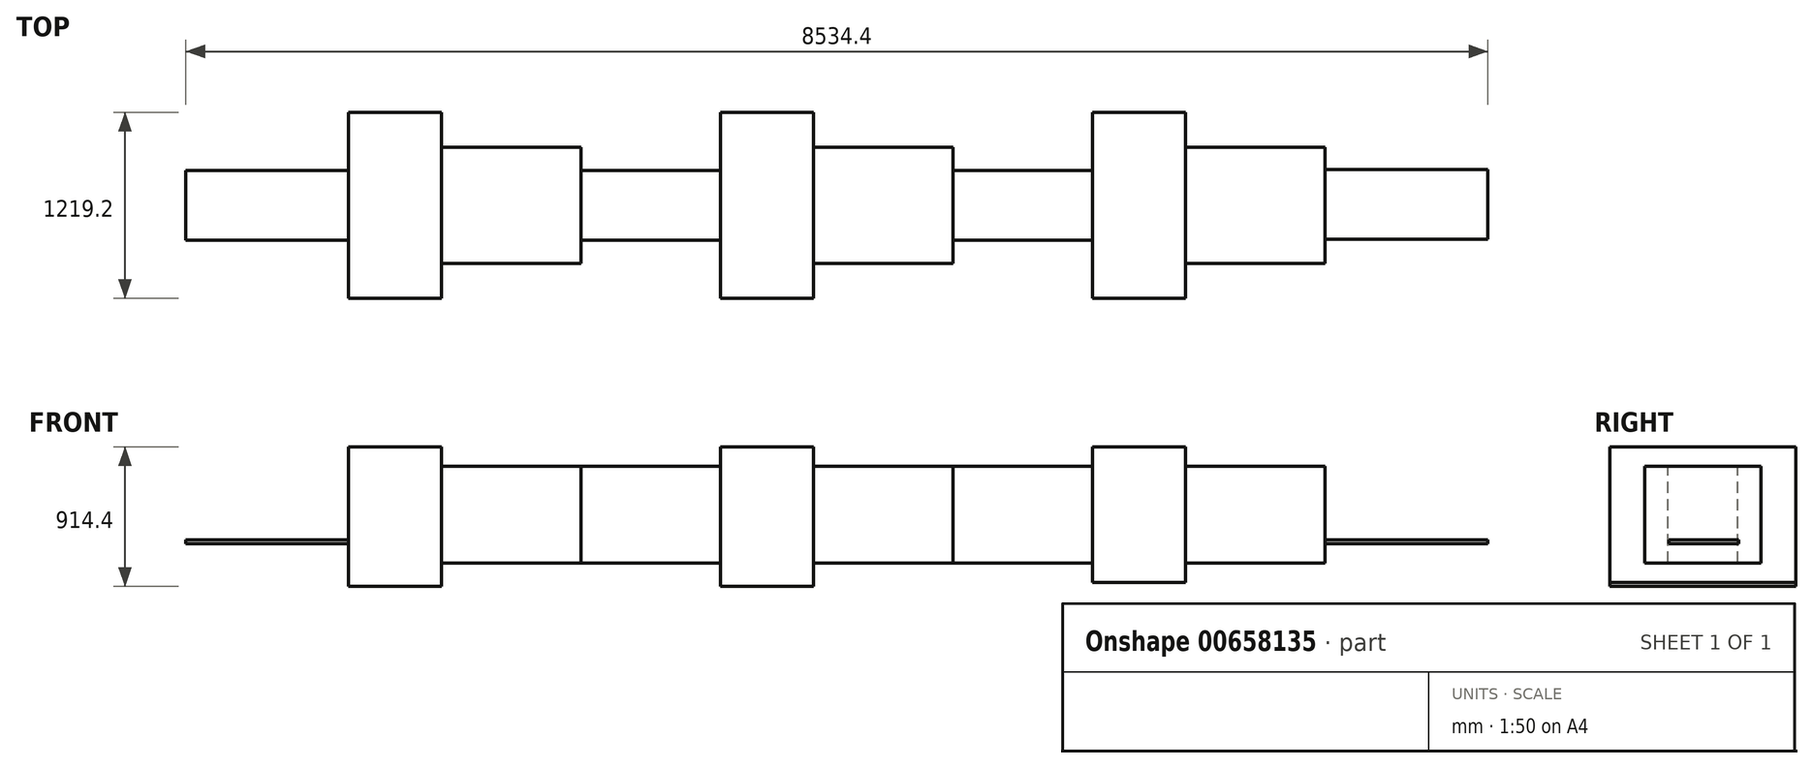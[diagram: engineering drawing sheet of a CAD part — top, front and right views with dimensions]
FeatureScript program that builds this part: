
annotation { "Feature Type Name" : "Feature", "Feature Type Description" : "" }
export const myFeature = defineFeature(function(context is Context, id is Id, definition is map)
    precondition{}
    {
        {
            var Q0;
            Q0=qCreatedBy(makeId("Top.planeOp"),FACE);
            var sketch = newSketch(context, id + "F0", { "sketchPlane" : qUnion([Q0])});
            skLineSegment(sketch, "E0.bottom", {"start": v(0, 0) * mm, "end": v(1066.8, 0) * mm});
            skLineSegment(sketch, "E0.top", {"start": v(0, 457.2) * mm, "end": v(1066.8, 457.2) * mm});
            skLineSegment(sketch, "E0.left", {"start": v(0, 0) * mm, "end": v(0, 457.2) * mm});
            skLineSegment(sketch, "E0.right", {"start": v(1066.8, 0) * mm, "end": v(1066.8, 457.2) * mm});
            skSolve(sketch);
        }
        {
            var Q0;
            Q0 = qSketchRegion(id + "F0", true);
            extrude(context, id + "F1", {"entities" : qUnion([Q0]), "depth" : 25.4 * mm, "offsetDistance" : 25.4 * mm});
        }
        {
            var Q0;
            Q0=makeQuery(id+"F1.opExtrude","CAP_FACE",FACE,{"disambiguationData":[OSD([sQuery(id+"F0.wireOp",EDGE,"E0.bottom"),sQuery(id+"F0.wireOp",EDGE,"E0.top"),sQuery(id+"F0.wireOp",EDGE,"E0.left"),sQuery(id+"F0.wireOp",EDGE,"E0.right")])],"isStart":false});
            var sketch = newSketch(context, id + "F2", { "sketchPlane" : qUnion([Q0])});
            skPoint(sketch, "E1", {"position": v(1066.8, -381) * mm});
            skLineSegment(sketch, "E2.bottom", {"start": v(1066.8, -381) * mm, "end": v(1676.4, -381) * mm});
            skLineSegment(sketch, "E2.top", {"start": v(1066.8, 838.2) * mm, "end": v(1676.4, 838.2) * mm});
            skLineSegment(sketch, "E2.left", {"start": v(1066.8, -381) * mm, "end": v(1066.8, 838.2) * mm});
            skLineSegment(sketch, "E2.right", {"start": v(1676.4, -381) * mm, "end": v(1676.4, 838.2) * mm});
            skSolve(sketch);
        }
        {
            var Q0;
            Q0 = qSketchRegion(id + "F2", true);
            extrude(context, id + "F3", {"entities" : qUnion([Q0]), "depth" : 609.6 * mm, "offsetDistance" : 25.4 * mm, "hasSecondDirection" : true, "secondDirectionOppositeDirection" : true, "secondDirectionDepth" : 304.8 * mm});
        }
        {
            var Q0;
            Q0=makeQuery(id+"F3.opExtrude","CAP_FACE",FACE,{"disambiguationData":[OSD([sQuery(id+"F2.wireOp",EDGE,"E2.bottom"),sQuery(id+"F2.wireOp",EDGE,"E2.top"),sQuery(id+"F2.wireOp",EDGE,"E2.left"),sQuery(id+"F2.wireOp",EDGE,"E2.right")])],"isStart":false});
            var sketch = newSketch(context, id + "F4", { "sketchPlane" : qUnion([Q0])});
            skLineSegment(sketch, "E3.right", {"start": v(2590.8, 0) * mm, "end": v(2590.8, 457.2) * mm});
            skPoint(sketch, "E4", {"position": v(2590.8, 0) * mm});
            skLineSegment(sketch, "E5.bottom", {"start": v(2590.8, 0) * mm, "end": v(3505.2, 0) * mm});
            skLineSegment(sketch, "E5.top", {"start": v(2590.8, 457.2) * mm, "end": v(3505.2, 457.2) * mm});
            skLineSegment(sketch, "E5.right", {"start": v(3505.2, 0) * mm, "end": v(3505.2, 457.2) * mm});
            skSolve(sketch);
        }
        {
            var Q0;
            Q0 = qSketchRegion(id + "F4", true);
            extrude(context, id + "F5", {"entities" : qUnion([Q0]), "oppositeDirection" : true, "depth" : 762 * mm, "offsetDistance" : 25.4 * mm, "hasSecondDirection" : true, "secondDirectionOppositeDirection" : true, "secondDirectionDepth" : 127 * mm});
        }
        {
            var Q0;
            Q0=makeQuery(id+"F3.opExtrude","CAP_FACE",FACE,{"disambiguationData":[OSD([sQuery(id+"F2.wireOp",EDGE,"E2.bottom"),sQuery(id+"F2.wireOp",EDGE,"E2.top"),sQuery(id+"F2.wireOp",EDGE,"E2.left"),sQuery(id+"F2.wireOp",EDGE,"E2.right")])],"isStart":false});
            var sketch = newSketch(context, id + "F6", { "sketchPlane" : qUnion([Q0])});
            skPoint(sketch, "E6", {"position": v(1676.4, -152.4) * mm});
            skPoint(sketch, "E7", {"position": v(1676.4, 228.6) * mm});
            skLineSegment(sketch, "E8.bottom", {"start": v(1676.4, -152.4) * mm, "end": v(2590.8, -152.4) * mm});
            skLineSegment(sketch, "E8.top", {"start": v(1676.4, 609.6) * mm, "end": v(2590.8, 609.6) * mm});
            skLineSegment(sketch, "E8.left", {"start": v(1676.4, -152.4) * mm, "end": v(1676.4, 609.6) * mm});
            skLineSegment(sketch, "E8.right", {"start": v(2590.8, -152.4) * mm, "end": v(2590.8, 609.6) * mm});
            skSolve(sketch);
        }
        {
            var Q0;
            Q0=makeQuery(id+"F6.imprint","IMPRINT",FACE,{"disambiguationData":[TD([[makeQuery(id+"F6.imprint","IMPRINT",EDGE,{"derivedFrom":sQuery(id+"F6.wireOp",EDGE,"E8.bottom")}),1.0]])]});
            extrude(context, id + "F7", {"entities" : qUnion([Q0]), "oppositeDirection" : true, "depth" : 762 * mm, "offsetDistance" : 25.4 * mm, "hasSecondDirection" : true, "secondDirectionOppositeDirection" : true, "secondDirectionDepth" : 127 * mm});
        }
        {
            var Q0;
            Q0=makeQuery(id+"F3.opExtrude","CAP_FACE",FACE,{"disambiguationData":[OSD([sQuery(id+"F2.wireOp",EDGE,"E2.bottom"),sQuery(id+"F2.wireOp",EDGE,"E2.top"),sQuery(id+"F2.wireOp",EDGE,"E2.left"),sQuery(id+"F2.wireOp",EDGE,"E2.right")])],"isStart":false});
            var sketch = newSketch(context, id + "F8", { "sketchPlane" : qUnion([Q0])});
            skPoint(sketch, "E9", {"position": v(3505.2, -381) * mm});
            skLineSegment(sketch, "E10.bottom", {"start": v(3505.2, -381) * mm, "end": v(4114.8, -381) * mm});
            skLineSegment(sketch, "E10.top", {"start": v(3505.2, 838.2) * mm, "end": v(4114.8, 838.2) * mm});
            skLineSegment(sketch, "E10.left", {"start": v(3505.2, -381) * mm, "end": v(3505.2, 838.2) * mm});
            skLineSegment(sketch, "E10.right", {"start": v(4114.8, -381) * mm, "end": v(4114.8, 838.2) * mm});
            skSolve(sketch);
        }
        {
            var Q0;
            Q0 = qSketchRegion(id + "F8", true);
            extrude(context, id + "F9", {"entities" : qUnion([Q0]), "oppositeDirection" : true, "depth" : 914.4 * mm, "offsetDistance" : 25.4 * mm});
        }
        {
            var Q0;
            Q0=makeQuery(id+"F9.opExtrude","CAP_FACE",FACE,{"disambiguationData":[OSD([sQuery(id+"F8.wireOp",EDGE,"E10.bottom"),sQuery(id+"F8.wireOp",EDGE,"E10.top"),sQuery(id+"F8.wireOp",EDGE,"E10.left"),sQuery(id+"F8.wireOp",EDGE,"E10.right")])],"isStart":true});
            var sketch = newSketch(context, id + "F10", { "sketchPlane" : qUnion([Q0])});
            skPoint(sketch, "E11", {"position": v(4114.8, -152.4) * mm});
            skPoint(sketch, "E12", {"position": v(4114.8, 228.6) * mm});
            skLineSegment(sketch, "E13.bottom", {"start": v(4114.8, -152.4) * mm, "end": v(5029.2, -152.4) * mm});
            skLineSegment(sketch, "E13.top", {"start": v(4114.8, 609.6) * mm, "end": v(5029.2, 609.6) * mm});
            skLineSegment(sketch, "E13.left", {"start": v(4114.8, -152.4) * mm, "end": v(4114.8, 609.6) * mm});
            skLineSegment(sketch, "E13.right", {"start": v(5029.2, -152.4) * mm, "end": v(5029.2, 609.6) * mm});
            skSolve(sketch);
        }
        {
            var Q0;
            Q0 = qSketchRegion(id + "F10", true);
            extrude(context, id + "F11", {"entities" : qUnion([Q0]), "oppositeDirection" : true, "depth" : 762 * mm, "offsetDistance" : 25.4 * mm, "hasSecondDirection" : true, "secondDirectionOppositeDirection" : true, "secondDirectionDepth" : 127 * mm});
        }
        {
            var Q0;
            Q0=makeQuery(id+"F11.opExtrude","CAP_FACE",FACE,{"disambiguationData":[OSD([sQuery(id+"F10.wireOp",EDGE,"E13.bottom"),sQuery(id+"F10.wireOp",EDGE,"E13.top"),sQuery(id+"F10.wireOp",EDGE,"E13.left"),sQuery(id+"F10.wireOp",EDGE,"E13.right")])],"isStart":true});
            var sketch = newSketch(context, id + "F12", { "sketchPlane" : qUnion([Q0])});
            skLineSegment(sketch, "E14.right", {"start": v(5029.2, 0) * mm, "end": v(5029.2, 457.2) * mm});
            skPoint(sketch, "E15", {"position": v(5029.2, 0) * mm});
            skLineSegment(sketch, "E16.bottom", {"start": v(5029.2, 0) * mm, "end": v(5943.6, 0) * mm});
            skLineSegment(sketch, "E16.top", {"start": v(5029.2, 457.2) * mm, "end": v(5943.6, 457.2) * mm});
            skLineSegment(sketch, "E16.right", {"start": v(5943.6, 0) * mm, "end": v(5943.6, 457.2) * mm});
            skSolve(sketch);
        }
        {
            var Q0;
            Q0 = qSketchRegion(id + "F12", true);
            extrude(context, id + "F13", {"entities" : qUnion([Q0]), "oppositeDirection" : true, "depth" : 635 * mm, "offsetDistance" : 25.4 * mm});
        }
        {
            var Q0;
            Q0=makeQuery(id+"F13.opExtrude","CAP_FACE",FACE,{"disambiguationData":[OSD([sQuery(id+"F12.wireOp",EDGE,"E16.bottom"),sQuery(id+"F12.wireOp",EDGE,"E16.top"),sQuery(id+"F12.wireOp",EDGE,"E14.right"),sQuery(id+"F12.wireOp",EDGE,"E16.right")])],"isStart":true});
            var sketch = newSketch(context, id + "F14", { "sketchPlane" : qUnion([Q0])});
            skPoint(sketch, "E17", {"position": v(5943.6, -381) * mm});
            skLineSegment(sketch, "E18.bottom", {"start": v(5943.6, -381) * mm, "end": v(6553.2, -381) * mm});
            skLineSegment(sketch, "E18.top", {"start": v(5943.6, 838.2) * mm, "end": v(6553.2, 838.2) * mm});
            skLineSegment(sketch, "E18.left", {"start": v(5943.6, -381) * mm, "end": v(5943.6, 838.2) * mm});
            skLineSegment(sketch, "E18.right", {"start": v(6553.2, -381) * mm, "end": v(6553.2, 838.2) * mm});
            skSolve(sketch);
        }
        {
            var Q0;
            Q0 = qSketchRegion(id + "F14", true);
            extrude(context, id + "F15", {"entities" : qUnion([Q0]), "depth" : 127 * mm, "offsetDistance" : 25.4 * mm, "hasSecondDirection" : true, "secondDirectionOppositeDirection" : true, "secondDirectionDepth" : 762 * mm});
        }
        {
            var Q0;
            Q0=makeQuery(id+"F15.opExtrude","CAP_FACE",FACE,{"disambiguationData":[OSD([sQuery(id+"F14.wireOp",EDGE,"E18.bottom"),sQuery(id+"F14.wireOp",EDGE,"E18.top"),sQuery(id+"F14.wireOp",EDGE,"E18.left"),sQuery(id+"F14.wireOp",EDGE,"E18.right")])],"isStart":false});
            var sketch = newSketch(context, id + "F16", { "sketchPlane" : qUnion([Q0])});
            skPoint(sketch, "E19", {"position": v(6553.2, -152.4) * mm});
            skPoint(sketch, "E20", {"position": v(6553.2, 228.6) * mm});
            skLineSegment(sketch, "E21.bottom", {"start": v(6553.2, -152.4) * mm, "end": v(7467.6, -152.4) * mm});
            skLineSegment(sketch, "E21.top", {"start": v(6553.2, 609.6) * mm, "end": v(7467.6, 609.6) * mm});
            skLineSegment(sketch, "E21.left", {"start": v(6553.2, -152.4) * mm, "end": v(6553.2, 609.6) * mm});
            skLineSegment(sketch, "E21.right", {"start": v(7467.6, -152.4) * mm, "end": v(7467.6, 609.6) * mm});
            skSolve(sketch);
        }
        {
            var Q0;
            Q0 = qSketchRegion(id + "F16", true);
            extrude(context, id + "F17", {"entities" : qUnion([Q0]), "oppositeDirection" : true, "depth" : 762 * mm, "offsetDistance" : 25.4 * mm, "hasSecondDirection" : true, "secondDirectionOppositeDirection" : true, "secondDirectionDepth" : 127 * mm});
        }
        {
            var Q0;
            Q0=makeQuery(id+"F17.opExtrude","CAP_FACE",FACE,{"disambiguationData":[OSD([sQuery(id+"F16.wireOp",EDGE,"E21.bottom"),sQuery(id+"F16.wireOp",EDGE,"E21.top"),sQuery(id+"F16.wireOp",EDGE,"E21.left"),sQuery(id+"F16.wireOp",EDGE,"E21.right")])],"isStart":true});
            var sketch = newSketch(context, id + "F18", { "sketchPlane" : qUnion([Q0])});
            skLineSegment(sketch, "E22.bottom", {"start": v(7467.6, 5.08) * mm, "end": v(8534.4, 5.08) * mm});
            skLineSegment(sketch, "E22.top", {"start": v(7467.6, 462.28) * mm, "end": v(8534.4, 462.28) * mm});
            skLineSegment(sketch, "E22.left", {"start": v(7467.6, 5.08) * mm, "end": v(7467.6, 462.28) * mm});
            skLineSegment(sketch, "E22.right", {"start": v(8534.4, 5.08) * mm, "end": v(8534.4, 462.28) * mm});
            skSolve(sketch);
        }
        {
            var Q0;
            Q0 = qSketchRegion(id + "F18", true);
            extrude(context, id + "F19", {"entities" : qUnion([Q0]), "oppositeDirection" : true, "depth" : 508 * mm, "offsetDistance" : 25.4 * mm, "hasSecondDirection" : true, "secondDirectionOppositeDirection" : true, "secondDirectionDepth" : 482.6 * mm});
        }
    });
